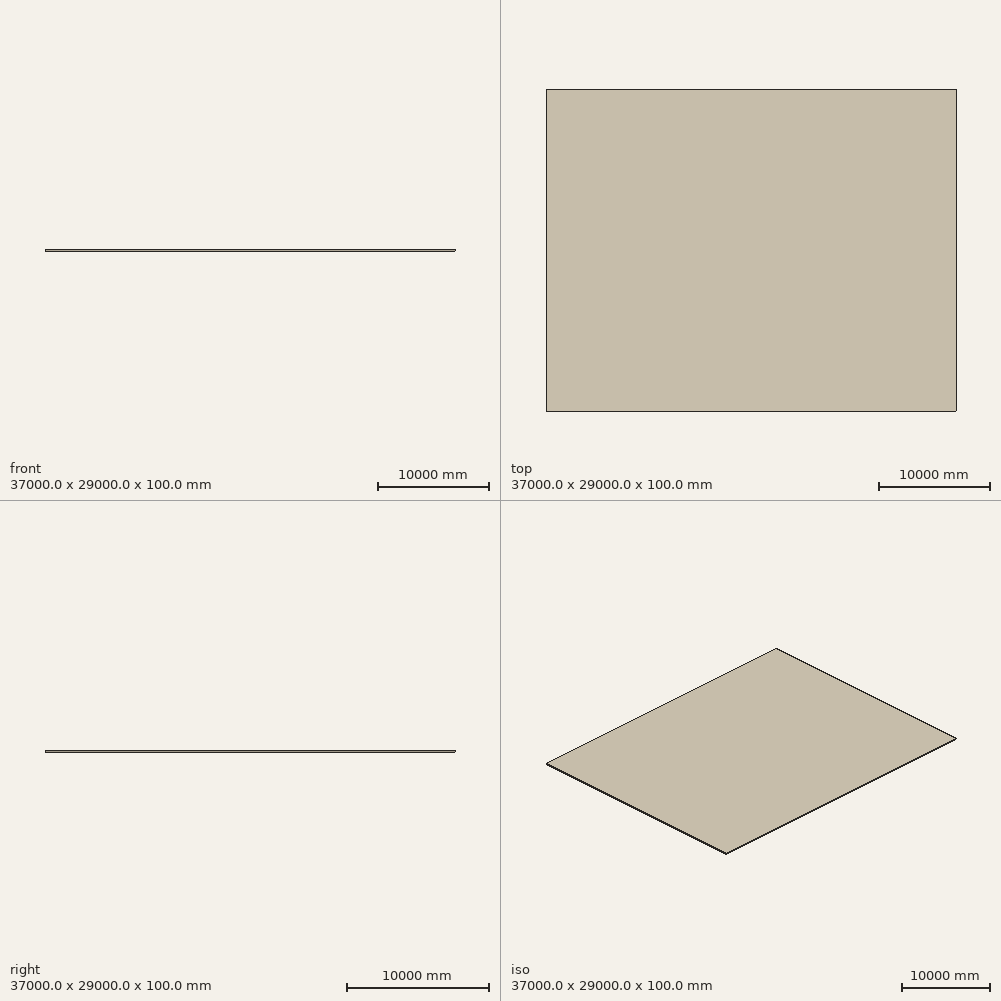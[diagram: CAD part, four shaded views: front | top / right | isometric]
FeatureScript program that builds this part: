
annotation { "Feature Type Name" : "Feature", "Feature Type Description" : "" }
export const myFeature = defineFeature(function(context is Context, id is Id, definition is map)
    precondition{}
    {
        {
            var Q0;
            Q0=qCreatedBy(makeId("Top.planeOp"),FACE);
            var sketch = newSketch(context, id + "F0", { "sketchPlane" : qUnion([Q0])});
            skLineSegment(sketch, "E0.bottom", {"start": v(18500, 14500) * mm, "end": v(-18500, 14500) * mm});
            skLineSegment(sketch, "E0.top", {"start": v(18500, -14500) * mm, "end": v(-18500, -14500) * mm});
            skLineSegment(sketch, "E0.left", {"start": v(18500, 14500) * mm, "end": v(18500, -14500) * mm});
            skLineSegment(sketch, "E0.right", {"start": v(-18500, 14500) * mm, "end": v(-18500, -14500) * mm});
            skPoint(sketch, "E0.middle", {"position": v(0, 0) * mm});
            skSolve(sketch);
        }
        {
            var Q0;
            Q0=makeQuery(id+"F0.imprint","IMPRINT",FACE,{"disambiguationData":[TD([[makeQuery(id+"F0.imprint","IMPRINT",EDGE,{"derivedFrom":sQuery(id+"F0.wireOp",EDGE,"E0.bottom")}),1.0]])]});
            extrude(context, id + "F1", {"entities" : qUnion([Q0]), "depth" : -100 * mm, "offsetDistance" : 25 * mm});
        }
    });
